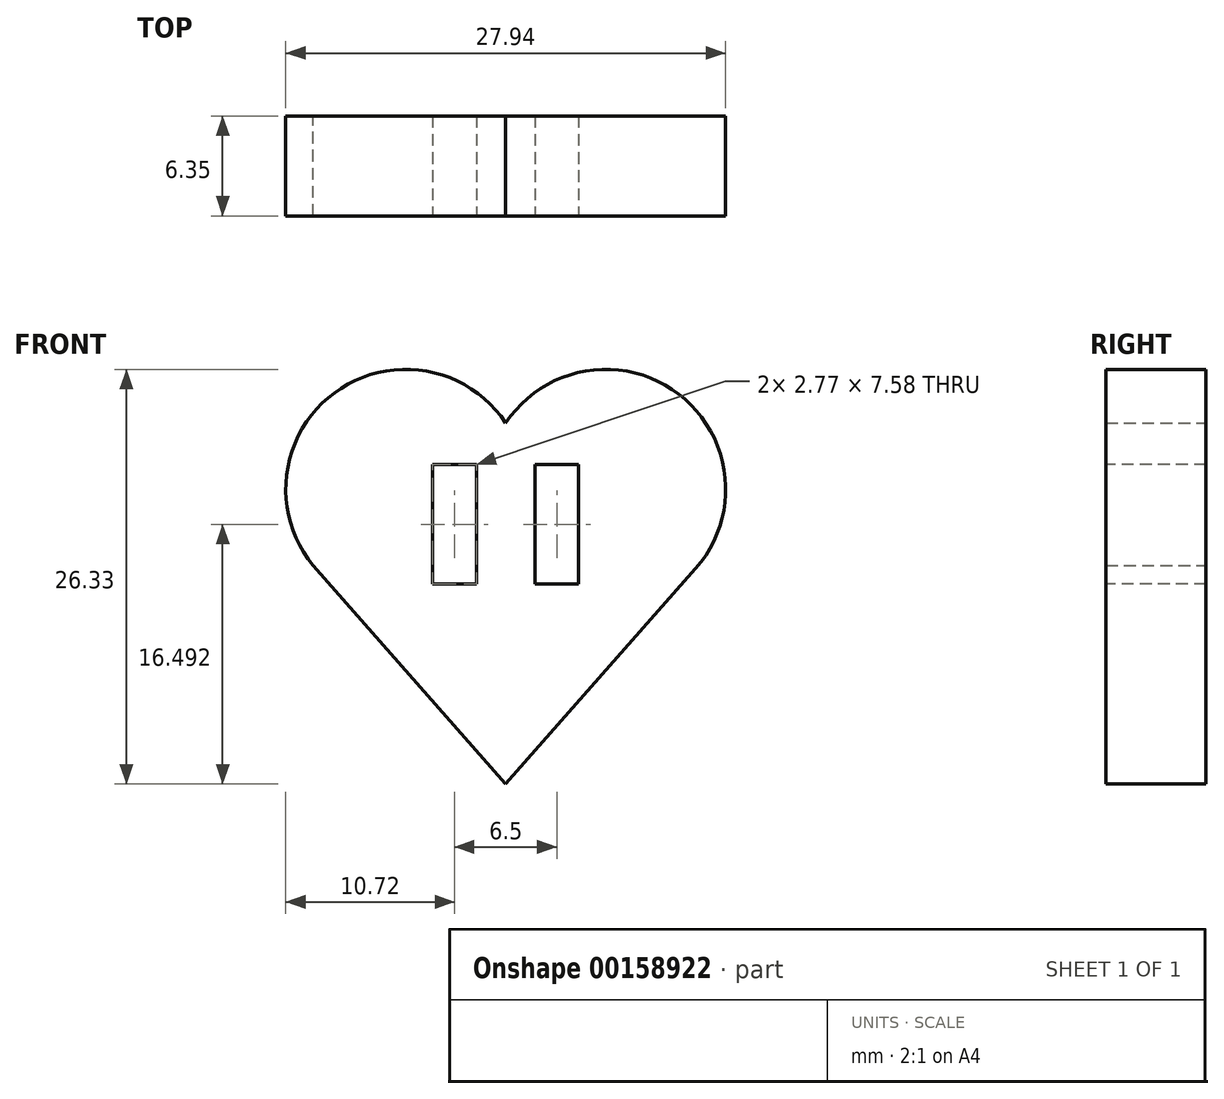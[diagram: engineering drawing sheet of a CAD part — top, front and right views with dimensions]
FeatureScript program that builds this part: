
annotation { "Feature Type Name" : "Feature", "Feature Type Description" : "" }
export const myFeature = defineFeature(function(context is Context, id is Id, definition is map)
    precondition{}
    {
        {
            var Q0;
            Q0=qCreatedBy(makeId("Front.planeOp"),FACE);
            var sketch = newSketch(context, id + "F0", { "sketchPlane" : qUnion([Q0])});
            skArc(sketch, "E0", {"start": v(0, 10.22) * mm, "mid": v(-11.09, 11.98) * mm, "end": v(-11.89, 0.78) * mm});
            skArc(sketch, "E1", {"start": v(12.06, 0.97) * mm, "mid": v(10.99, 12.06) * mm, "end": v(0, 10.22) * mm});
            skLineSegment(sketch, "E2", {"start": v(0, -12.7) * mm, "end": v(-12.23, 1.17) * mm});
            skLineSegment(sketch, "E3", {"start": v(0, -12.7) * mm, "end": v(12.28, 1.21) * mm});
            skPoint(sketch, "E4.end.orphan", {"position": v(0, 6.01) * mm});
            skSolve(sketch);
        }
        {
            var Q0;
            {var subQ6=sQuery(id+"F0.wireOp",EDGE,"E1");Q0=makeQuery(id+"F0.imprint","IMPRINT",FACE,{"disambiguationData":[TD([[makeQuery(id+"F0.imprint","IMPRINT",EDGE,{"derivedFrom":subQ6}),1.0]])]});}
            extrude(context, id + "F1", {"entities" : qUnion([Q0]), "depth" : 6.35 * mm});
        }
        {
            var Q0;
            Q0=makeQuery(id+"F1.opExtrude","CAP_FACE",FACE,{"disambiguationData":[OSD([sQuery(id+"F0.wireOp",EDGE,"E0"),sQuery(id+"F0.wireOp",EDGE,"E1"),sQuery(id+"F0.wireOp",EDGE,"E2"),sQuery(id+"F0.wireOp",EDGE,"E3")])],"isStart":false});
            var sketch = newSketch(context, id + "F2", { "sketchPlane" : qUnion([Q0])});
            skLineSegment(sketch, "E5.bottom", {"start": v(-1.86, 0) * mm, "end": v(-4.64, 0) * mm});
            skLineSegment(sketch, "E5.top", {"start": v(-1.86, 7.58) * mm, "end": v(-4.64, 7.58) * mm});
            skLineSegment(sketch, "E5.left", {"start": v(-1.86, 0) * mm, "end": v(-1.86, 7.58) * mm});
            skLineSegment(sketch, "E5.right", {"start": v(-4.64, 0) * mm, "end": v(-4.64, 7.58) * mm});
            skLineSegment(sketch, "E6.MirrorCS", {"start": v(1.86, 0) * mm, "end": v(1.86, 7.58) * mm});
            skLineSegment(sketch, "E7.MirrorCS", {"start": v(1.86, 0) * mm, "end": v(4.64, 0) * mm});
            skLineSegment(sketch, "E8.MirrorCS", {"start": v(4.64, 0) * mm, "end": v(4.64, 7.58) * mm});
            skLineSegment(sketch, "E9.MirrorCS", {"start": v(1.86, 7.58) * mm, "end": v(4.64, 7.58) * mm});
            skSolve(sketch);
        }
        {
            var Q0;
            Q0 = qSketchRegion(id + "F2", true);
            extrude(context, id + "F3", {"entities" : qUnion([Q0]), "operationType" : NewBodyOperationType.REMOVE, "oppositeDirection" : true, "depth" : 25.4 * mm});
        }
    });
